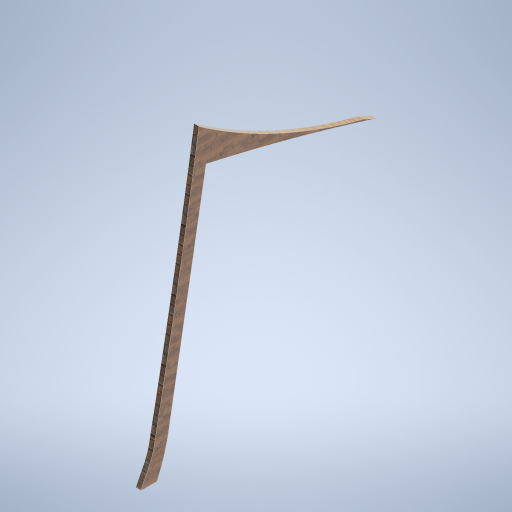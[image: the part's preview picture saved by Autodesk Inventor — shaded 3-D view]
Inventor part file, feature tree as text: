
AUTODESK INVENTOR PART (.ipt)
format: ipt  version: 2024.2 (Build 282272000, 272)  size: 314,368 bytes
history: native  units: mm
features: extrude x1, fillet x1, sketch x1
ambient origin geometry x8: Origin, YZ Plane, XZ Plane, XY Plane, X Axis, Y Axis, Z Axis, Center Point
bodies: Body1 (feature_tree)
feature tree (3):
  extrude  "Extrusion2"  Depth=10.0mm
  fillet  "Fillet1"  [1 undecoded]
  sketch  "Sketch1"  dims[d0=5000.0mm d1=29.670597mm d4=75.0deg d9=120000.0mm d11=100.0mm d12=0.0mm d13=40000.0mm d14=10.0mm]
note: 1 required parameter value undecoded (feature->parameter linkage not recoverable at this tier; creation-order binding heuristic only, values carry confidence <= 0.55)
